FCSTD DOCUMENT  (FreeCAD 0.16R)
Label: BitHolderV1
License: All rights reserved
LicenseURL: http://en.wikipedia.org/wiki/All_rights_reserved
objects: Sketcher::SketchObject×1
note: 1 computed .brp shape members not serialized (recipe doc carries the construction recipe); baked Part::Feature solids carry a one-line shape summary decoded from their .brp

FEATURE [Sketcher::SketchObject] Sketch
  sketch-geometry (4):
    g0: LineSegment StartX=-101.457 StartY=64.1766 StartZ=0 EndX=198.543 EndY=64.1766 EndZ=0
    g1: LineSegment StartX=198.543 StartY=64.1766 StartZ=0 EndX=198.543 EndY=-35.8234 EndZ=0
    g2: LineSegment StartX=198.543 StartY=-35.8234 StartZ=0 EndX=-101.457 EndY=-35.8234 EndZ=0
    g3: LineSegment StartX=-101.457 StartY=-35.8234 StartZ=0 EndX=-101.457 EndY=64.1766 EndZ=0
  constraints (10):
    c: Coincident(g0,g1)
    c: Coincident(g1,g2)
    c: Coincident(g2,g3)
    c: Coincident(g3,g0)
    c: Horizontal(g0)
    c: Horizontal(g2)
    c: Vertical(g1)
    c: Vertical(g3)
    c: DistanceX(g0,g0) = 300
    c: DistanceY(g3,g3) = 100
